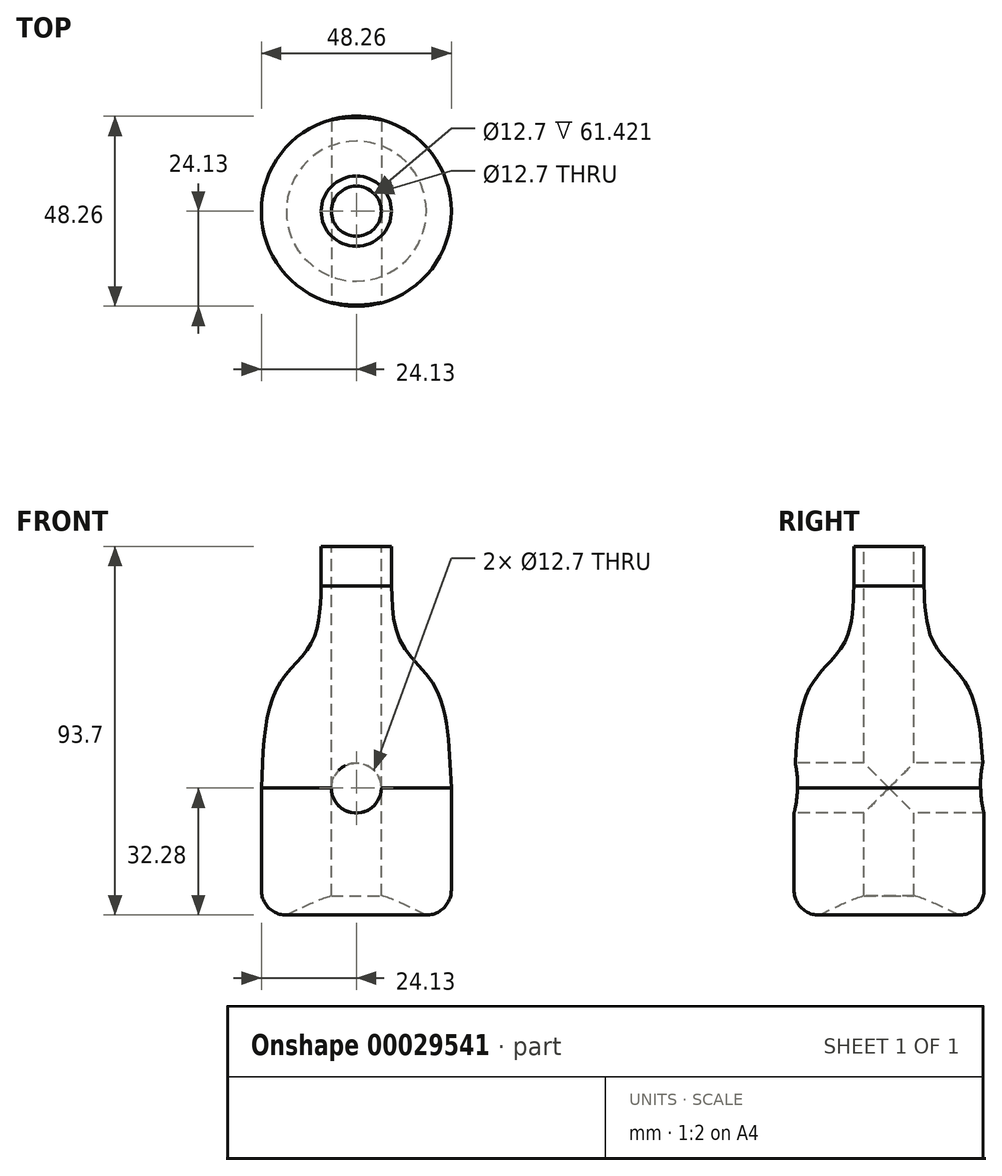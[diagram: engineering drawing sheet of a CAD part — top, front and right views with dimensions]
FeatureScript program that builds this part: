
annotation { "Feature Type Name" : "Feature", "Feature Type Description" : "" }
export const myFeature = defineFeature(function(context is Context, id is Id, definition is map)
    precondition{}
    {
        {
            var Q0;
            Q0=qCreatedBy(makeId("Front.planeOp"),FACE);
            var sketch = newSketch(context, id + "F0", { "sketchPlane" : qUnion([Q0])});
            skLineSegment(sketch, "E0", {"start": v(0, 61.42) * mm, "end": v(8.92, 61.42) * mm});
            skLineSegment(sketch, "E1", {"start": v(8.92, 61.42) * mm, "end": v(8.92, 51.37) * mm});
            skFitSpline(sketch, "E2", {"points": [v(8.92, 51.37) * mm, v(11.43, 36.8) * mm, v(20.22, 25.25) * mm, v(24.13, 0) * mm], "startDerivative": vector(1.67, -52.15) * mm, "endDerivative": vector(3.55, -71.66) * mm});
            skLineSegment(sketch, "E3", {"start": v(24.13, 0) * mm, "end": v(24.13, -25.93) * mm});
            skLineSegment(sketch, "E4", {"start": v(0, -25.93) * mm, "end": v(0, 61.42) * mm});
            skPoint(sketch, "E5.visualSharp", {"position": v(24.13, -32.28) * mm});
            skArc(sketch, "E5.filletArc", {"start": v(17.78, -32.28) * mm, "mid": v(22.27, -30.42) * mm, "end": v(24.13, -25.93) * mm});
            skFitSpline(sketch, "E6", {"points": [v(17.78, -32.28) * mm, v(7.66, -27.76) * mm, v(0, -25.93) * mm], "startDerivative": vector(-19.42, 9.48) * mm, "endDerivative": vector(-16.33, 3.03) * mm});
            skPoint(sketch, "E7", {"position": v(0, -32.28) * mm});
            skPoint(sketch, "E8", {"position": v(4.4, -32.28) * mm});
            skSolve(sketch);
        }
        {
            var Q0;
            Q0=makeQuery(id+"F0.imprint","IMPRINT",FACE,{"disambiguationData":[TD([[makeQuery(id+"F0.imprint","IMPRINT",EDGE,{"derivedFrom":sQuery(id+"F0.wireOp",EDGE,"E0")}),-1.0]])]});
            var Q1;
            Q1=sQuery(id+"F0.wireOp",EDGE,"E4");
            revolve(context, id + "F1", {"entities" : qUnion([Q0]), "axis" : qUnion([Q1]), "revolveType" : RevolveType.FULL});
        }
        {
            var Q0;
            Q0=makeQuery(id+"F1.opRevolve","SWEPT_FACE",FACE,{"disambiguationData":[OSD([sQuery(id+"F0.wireOp",EDGE,"E0")])]});
            var sketch = newSketch(context, id + "F2", { "sketchPlane" : qUnion([Q0])});
            skPoint(sketch, "E9", {"position": v(0, 0) * mm});
            skSolve(sketch);
        }
        {
            var Q0;
            Q0=sQuery(id+"F2.wireOp",VERTEX,"E9");
            var Q1;
            Q1=makeQuery(id+"F1.opRevolve","SWEPT_BODY",BODY,{"disambiguationData":[OSD([sQuery(id+"F0.wireOp",EDGE,"E0"),sQuery(id+"F0.wireOp",EDGE,"E1"),sQuery(id+"F0.wireOp",EDGE,"E2"),sQuery(id+"F0.wireOp",EDGE,"E3"),sQuery(id+"F0.wireOp",EDGE,"E4"),sQuery(id+"F0.wireOp",EDGE,"E5.filletArc"),sQuery(id+"F0.wireOp",EDGE,"E6")])]});
            hole(context, id + "F3", {"style" : HoleStyle.SIMPLE, "holeDiameter" : 12.7 * mm, "endStyle" : HoleEndStyle.THROUGH, "locations" : qUnion([Q0]), "scope" : qUnion([Q1])});
        }
        {
            var Q0;
            Q0=qCreatedBy(makeId("Front.planeOp"),FACE);
            cPlane(context, id + "F4", {"entities" : qUnion([Q0]), "cplaneType" : CPlaneType.OFFSET, "offset" : 25.4 * mm, "width" : 152.4 * mm, "height" : 152.4 * mm});
        }
        {
            var Q0;
            Q0=qCreatedBy(id+"F4.planeOp",FACE);
            var sketch = newSketch(context, id + "F5", { "sketchPlane" : qUnion([Q0])});
            skPoint(sketch, "E10", {"position": v(0, 0) * mm});
            skSolve(sketch);
        }
        {
            var Q0;
            Q0=sQuery(id+"F5.wireOp",VERTEX,"E10");
            var Q1;
            Q1=makeQuery(id+"F1.opRevolve","SWEPT_BODY",BODY,{"disambiguationData":[OSD([sQuery(id+"F0.wireOp",EDGE,"E0"),sQuery(id+"F0.wireOp",EDGE,"E1"),sQuery(id+"F0.wireOp",EDGE,"E2"),sQuery(id+"F0.wireOp",EDGE,"E3"),sQuery(id+"F0.wireOp",EDGE,"E4"),sQuery(id+"F0.wireOp",EDGE,"E5.filletArc"),sQuery(id+"F0.wireOp",EDGE,"E6")])]});
            hole(context, id + "F6", {"style" : HoleStyle.SIMPLE, "holeDiameter" : 12.7 * mm, "endStyle" : HoleEndStyle.THROUGH, "locations" : qUnion([Q0]), "scope" : qUnion([Q1])});
        }
    });
